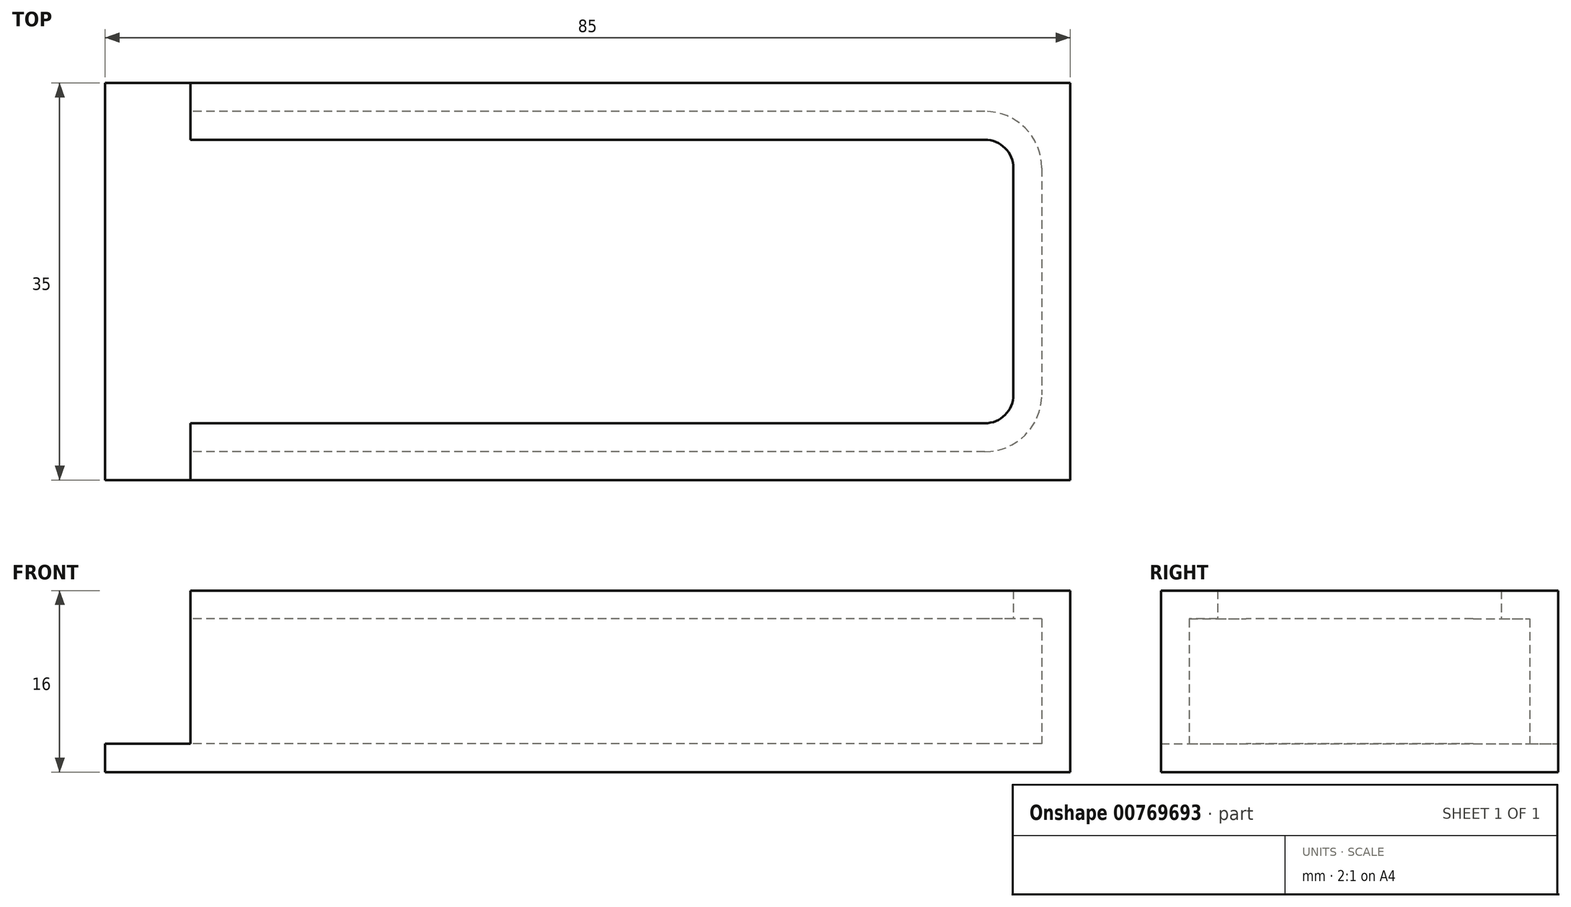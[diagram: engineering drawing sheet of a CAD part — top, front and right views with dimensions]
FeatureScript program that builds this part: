
annotation { "Feature Type Name" : "Feature", "Feature Type Description" : "" }
export const myFeature = defineFeature(function(context is Context, id is Id, definition is map)
    precondition{}
    {
        {
            var Q0;
            Q0=qCreatedBy(makeId("Top.planeOp"),FACE);
            var sketch = newSketch(context, id + "F0", { "sketchPlane" : qUnion([Q0])});
            skLineSegment(sketch, "E0.bottom", {"start": v(40, 15) * mm, "end": v(35, 15) * mm, "construction": true});
            skLineSegment(sketch, "E0.top", {"start": v(40, -15) * mm, "end": v(35, -15) * mm, "construction": true});
            skLineSegment(sketch, "E0.left", {"start": v(40, 15) * mm, "end": v(40, 10) * mm});
            skLineSegment(sketch, "E0.right", {"start": v(-40, 15) * mm, "end": v(-40, 10) * mm, "construction": true});
            skPoint(sketch, "E0.middle", {"position": v(0, 0) * mm});
            skArc(sketch, "E1", {"start": v(-35, 15) * mm, "mid": v(-38.54, 13.54) * mm, "end": v(-40, 10) * mm});
            skArc(sketch, "E2", {"start": v(-40, -10) * mm, "mid": v(-38.54, -13.54) * mm, "end": v(-35, -15) * mm});
            skArc(sketch, "E3", {"start": v(35, -15) * mm, "mid": v(38.54, -13.54) * mm, "end": v(40, -10) * mm});
            skArc(sketch, "E4", {"start": v(40, 10) * mm, "mid": v(38.54, 13.54) * mm, "end": v(35, 15) * mm});
            skLineSegment(sketch, "E5", {"start": v(-35, 15) * mm, "end": v(-40, 15) * mm, "construction": true});
            skLineSegment(sketch, "E6", {"start": v(-40, 10) * mm, "end": v(-40, -10) * mm});
            skLineSegment(sketch, "E7", {"start": v(-35, -15) * mm, "end": v(-35, -15) * mm});
            skLineSegment(sketch, "E8", {"start": v(-40, -10) * mm, "end": v(-40, -15) * mm});
            skLineSegment(sketch, "E9", {"start": v(35, 15) * mm, "end": v(-35, 15) * mm});
            skLineSegment(sketch, "E10", {"start": v(40, 10) * mm, "end": v(40, -10) * mm});
            skLineSegment(sketch, "E11", {"start": v(40, -10) * mm, "end": v(40, -15) * mm});
            skLineSegment(sketch, "E12", {"start": v(35, -15) * mm, "end": v(-35, -15) * mm});
            skLineSegment(sketch, "E13", {"start": v(-35, -15) * mm, "end": v(-40, -15) * mm, "construction": true});
            skLineSegment(sketch, "E14.bottom", {"start": v(42.5, 17.5) * mm, "end": v(-42.5, 17.5) * mm});
            skLineSegment(sketch, "E14.top", {"start": v(42.5, -17.5) * mm, "end": v(-42.5, -17.5) * mm});
            skLineSegment(sketch, "E14.left", {"start": v(42.5, 17.5) * mm, "end": v(42.5, -17.5) * mm});
            skLineSegment(sketch, "E14.right", {"start": v(-42.5, 17.5) * mm, "end": v(-42.5, -17.5) * mm});
            skSolve(sketch);
        }
        {
            var Q0;
            Q0=makeQuery(id+"F0.imprint","IMPRINT",FACE,{"disambiguationData":[TD([[makeQuery(id+"F0.imprint","IMPRINT",EDGE,{"derivedFrom":sQuery(id+"F0.wireOp",EDGE,"E1")}),1.0]])]});
            var Q1;
            Q1=makeQuery(id+"F0.imprint","IMPRINT",FACE,{"disambiguationData":[TD([[makeQuery(id+"F0.imprint","IMPRINT",EDGE,{"derivedFrom":sQuery(id+"F0.wireOp",EDGE,"E1")}),-1.0]])]});
            extrude(context, id + "F1", {"entities" : qUnion([Q0, Q1]), "oppositeDirection" : true, "depth" : 2.5 * mm, "offsetDistance" : 25 * mm});
        }
        {
            var Q0;
            Q0=makeQuery(id+"F0.imprint","IMPRINT",FACE,{"disambiguationData":[TD([[makeQuery(id+"F0.imprint","IMPRINT",EDGE,{"derivedFrom":sQuery(id+"F0.wireOp",EDGE,"E1")}),-1.0]])]});
            extrude(context, id + "F2", {"entities" : qUnion([Q0]), "operationType" : NewBodyOperationType.ADD, "depth" : 11 * mm, "offsetDistance" : 25 * mm});
        }
        {
            var Q0;
            Q0=makeQuery(id+"F2.opExtrude","CAP_FACE",FACE,{"disambiguationData":[OSD([sQuery(id+"F0.wireOp",EDGE,"E1"),sQuery(id+"F0.wireOp",EDGE,"E2"),sQuery(id+"F0.wireOp",EDGE,"E3"),sQuery(id+"F0.wireOp",EDGE,"E4"),sQuery(id+"F0.wireOp",EDGE,"E6"),sQuery(id+"F0.wireOp",EDGE,"E9"),sQuery(id+"F0.wireOp",EDGE,"E10"),sQuery(id+"F0.wireOp",EDGE,"E12"),sQuery(id+"F0.wireOp",EDGE,"E14.bottom"),sQuery(id+"F0.wireOp",EDGE,"E14.top"),sQuery(id+"F0.wireOp",EDGE,"E14.left"),sQuery(id+"F0.wireOp",EDGE,"E14.right")])],"isStart":false});
            var sketch = newSketch(context, id + "F3", { "sketchPlane" : qUnion([Q0])});
            skLineSegment(sketch, "E15", {"start": v(-35, 17.5) * mm, "end": v(-35, -17.5) * mm});
            skSolve(sketch);
        }
        {
            var Q0;
            {var subQ1=makeQuery(id+"F2.opExtrude","CAP_EDGE",EDGE,{"disambiguationData":[OSD([sQuery(id+"F0.wireOp",EDGE,"E1")])],"isStart":false});Q0=makeQuery(id+"F3.imprint","IMPRINT",FACE,{"disambiguationData":[TD([[makeQuery(id+"F3.imprint","IMPRINT",EDGE,{"derivedFrom":subQ1}),-1.0]])]});}
            var Q1;
            Q1=makeQuery(id+"F1.opExtrude","CAP_FACE",FACE,{"disambiguationData":[OSD([sQuery(id+"F0.wireOp",EDGE,"E14.bottom"),sQuery(id+"F0.wireOp",EDGE,"E14.top"),sQuery(id+"F0.wireOp",EDGE,"E14.left"),sQuery(id+"F0.wireOp",EDGE,"E14.right")])],"isStart":true});
            extrude(context, id + "F4", {"entities" : qUnion([Q0]), "operationType" : NewBodyOperationType.REMOVE, "endBound" : BoundingType.UP_TO_SURFACE, "oppositeDirection" : true, "depth" : 25 * mm, "endBoundEntityFace" : qUnion([Q1]), "offsetDistance" : 25 * mm});
        }
        {
            var Q0;
            Q0=makeQuery(id+"F2.opExtrude","CAP_FACE",FACE,{"disambiguationData":[OSD([sQuery(id+"F0.wireOp",EDGE,"E1"),sQuery(id+"F0.wireOp",EDGE,"E2"),sQuery(id+"F0.wireOp",EDGE,"E3"),sQuery(id+"F0.wireOp",EDGE,"E4"),sQuery(id+"F0.wireOp",EDGE,"E6"),sQuery(id+"F0.wireOp",EDGE,"E9"),sQuery(id+"F0.wireOp",EDGE,"E10"),sQuery(id+"F0.wireOp",EDGE,"E12"),sQuery(id+"F0.wireOp",EDGE,"E14.bottom"),sQuery(id+"F0.wireOp",EDGE,"E14.top"),sQuery(id+"F0.wireOp",EDGE,"E14.left"),sQuery(id+"F0.wireOp",EDGE,"E14.right")])],"isStart":false});
            var sketch = newSketch(context, id + "F5", { "sketchPlane" : qUnion([Q0])});
            skLineSegment(sketch, "E16.0", {"start": v(35, 12.5) * mm, "end": v(-35, 12.5) * mm});
            skArc(sketch, "E16.1", {"start": v(37.5, 10) * mm, "mid": v(36.77, 11.77) * mm, "end": v(35, 12.5) * mm});
            skLineSegment(sketch, "E16.3", {"start": v(37.5, 10) * mm, "end": v(37.5, -10) * mm});
            skLineSegment(sketch, "E16.6", {"start": v(35, -12.5) * mm, "end": v(-35, -12.5) * mm});
            skArc(sketch, "E16.7", {"start": v(35, -12.5) * mm, "mid": v(36.77, -11.77) * mm, "end": v(37.5, -10) * mm});
            skLineSegment(sketch, "E17", {"start": v(-35, -12.5) * mm, "end": v(-35, -15) * mm});
            skLineSegment(sketch, "E18", {"start": v(-35, 12.5) * mm, "end": v(-35, 15) * mm});
            skSolve(sketch);
        }
        {
            var Q0;
            Q0=makeQuery(id+"F5.imprint","IMPRINT",FACE,{"disambiguationData":[TD([[makeQuery(id+"F5.imprint","IMPRINT",EDGE,{"derivedFrom":sQuery(id+"F5.wireOp",EDGE,"E16.0")}),-1.0]])]});
            var Q1;
            Q1=makeQuery(id+"F5.imprint","IMPRINT",FACE,{"disambiguationData":[TD([[makeQuery(id+"F5.imprint","IMPRINT",EDGE,{"derivedFrom":makeQuery(id+"F2.opExtrude","CAP_EDGE",EDGE,{"disambiguationData":[OSD([sQuery(id+"F0.wireOp",EDGE,"E3")])],"isStart":false})}),-1.0]])]});
            extrude(context, id + "F6", {"entities" : qUnion([Q0, Q1]), "operationType" : NewBodyOperationType.ADD, "depth" : 2.5 * mm, "offsetDistance" : 25 * mm});
        }
    });
